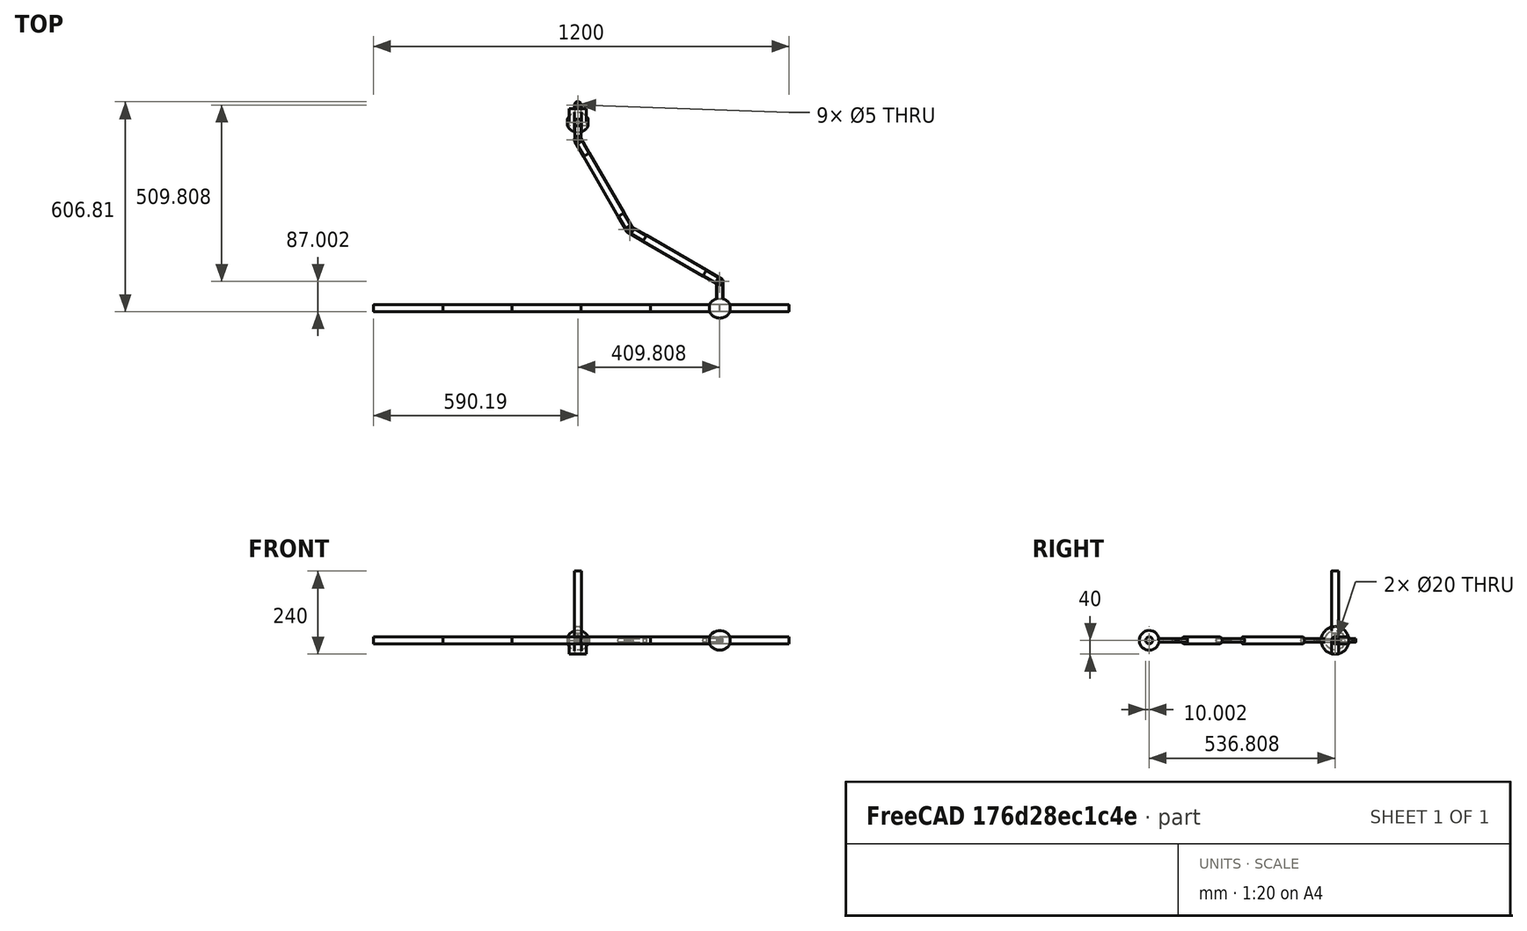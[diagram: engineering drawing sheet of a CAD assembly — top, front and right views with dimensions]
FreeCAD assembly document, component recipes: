
FREECAD ASSEMBLY — COMPONENT RECIPES ("Demo2Bodies")

This assembly document has 7 components, labeled P0..P6 below (a component is one placed body or linked part). 7 of them carry a construction recipe — the FreeCAD feature program that regenerates the part from scratch, quoted from this document or its linked companion documents; the rest are supplied as boundary geometry only. No exploded tour is included for this assembly.
COMPONENT P0 — recipe-attached ("Weight", modeled in this document).
Construction recipe (the document's own serialized feature program — sketch geometry with constraints, then the solid features built on it; lengths are millimeters unless a unit is written):

FEATURE [Sketcher::SketchObject] Sketch
  FullyConstrained = true
  MapMode = 5
  Support = -> [XY_Plane]
  sketch-geometry (2):
    g0: LineSegment StartX=-30 StartY=10 StartZ=0 EndX=30 EndY=10 EndZ=0
    g1: ArcOfCircle CenterX=0 CenterY=-5 CenterZ=0 NormalX=0 NormalY=0 NormalZ=1 AngleXU=0 Radius=33.541 StartAngle=0.463648 EndAngle=2.67795
  constraints (7):
    c: Horizontal(g0)
    c: DistanceY(g-1,g0) = 10
    c: DistanceX(g-1,g0) = 30
    c: PointOnObject(g1,g-2)
    c: DistanceY(g1,g-1) = 5
    c: Coincident(g1,g0)
    c: Coincident(g1,g0)
FEATURE [PartDesign::Revolution] Revolution
  Angle = 360
  Axis = (1,0,0)
  Base = (0,0,0)
  Profile = -> Sketch
  ReferenceAxis = -> Sketch [H_Axis]
FEATURE [PartDesign::CoordinateSystem] WeightTop
  AttacherType = Attacher::AttachEngine3D
  MapMode = 11
  Placement = pos=(30,-1.8e-15,0) rot=(0.707107,0,0.707107;3.14159rad)
  Support = -> [Revolution]
FEATURE [PartDesign::CoordinateSystem] WeightBot
  AttacherType = Attacher::AttachEngine3D
  MapMode = 11
  Placement = pos=(-30,0,0) rot=(0.707107,0,0.707107;3.14159rad)
  Support = -> [Revolution]
FEATURE [PartDesign::CoordinateSystem] WeightLCS
  AttacherType = Attacher::AttachEngine3D
  MapMode = 2
  Support = -> [Body003]
FEATURE [PartDesign::Body] Body  label="Weight"
  Group = -> [Sketch,Revolution,WeightLCS,WeightTop,WeightBot]
  Origin = -> Origin
  Tip = -> Revolution
COMPONENT P1 — recipe-attached ("Rod", modeled in this document).
Construction recipe (the document's own serialized feature program — sketch geometry with constraints, then the solid features built on it; lengths are millimeters unless a unit is written):

FEATURE [Sketcher::SketchObject] Sketch001
  FullyConstrained = true
  MapMode = 5
  Support = -> [XY_Plane001]
  sketch-geometry (1):
    g0: Circle CenterX=0 CenterY=0 CenterZ=0 NormalX=0 NormalY=0 NormalZ=1 AngleXU=0 Radius=10
  constraints (2):
    c: Coincident(g0,g-1)
    c: Diameter(g0) = 20
FEATURE [PartDesign::Pad] Pad
  Direction = (0,0,1)
  Length = 200
  Length2 = 10
  Profile = -> Sketch001
  ReferenceAxis = -> Sketch001 [N_Axis]
  Type = 0
FEATURE [PartDesign::CoordinateSystem] RodTop
  AttacherType = Attacher::AttachEngine3D
  MapMode = 11
  Placement = pos=(0,0,200) rot=(0,0,1;1.5708rad)
  Support = -> [Pad]
FEATURE [PartDesign::CoordinateSystem] RodBottom
  AttacherType = Attacher::AttachEngine3D
  MapMode = 11
  Placement = pos=(0,0,0) rot=(0,0,1;1.5708rad)
  Support = -> [Pad]
FEATURE [PartDesign::Body] Body001  label="Rod"
  Group = -> [Sketch001,Pad,RodTop,RodBottom]
  Origin = -> Origin001
  Tip = -> Pad
COMPONENT P2 — recipe-attached ("LugBody", modeled in this document).
Construction recipe (the document's own serialized feature program — sketch geometry with constraints, then the solid features built on it; lengths are millimeters unless a unit is written):

FEATURE [Sketcher::SketchObject] Sketch002
  FullyConstrained = true
  MapMode = 5
  Support = -> [XY_Plane002]
  sketch-geometry (5):
    g0: LineSegment StartX=-10 StartY=0 StartZ=0 EndX=-10 EndY=50 EndZ=0
    g1: ArcOfCircle CenterX=0 CenterY=50 CenterZ=0 NormalX=0 NormalY=0 NormalZ=1 AngleXU=0 Radius=10 StartAngle=1e-16 EndAngle=3.14159
    g2: LineSegment StartX=10 StartY=50 StartZ=0 EndX=10 EndY=0 EndZ=0
    g3: LineSegment StartX=10 StartY=0 StartZ=0 EndX=-10 EndY=0 EndZ=0
    g4: Circle CenterX=0 CenterY=50 CenterZ=0 NormalX=0 NormalY=0 NormalZ=1 AngleXU=0 Radius=2.5
  constraints (13):
    c: PointOnObject(g0,g-1)
    c: Vertical(g0)
    c: Tangent(g0,g1) = 1.5708
    c: Tangent(g1,g2) = 1.5708
    c: Coincident(g2,g3)
    c: Coincident(g3,g0)
    c: Horizontal(g3)
    c: PointOnObject(g1,g-2)
    c: Vertical(g2)
    c: Diameter(g1) = 20
    c: Distance(g2) = 50
    c: Coincident(g4,g1)
    c: Diameter(g4) = 5
FEATURE [PartDesign::Pad] Pad001
  Direction = (0,0,1)
  Length = 10
  Length2 = 10
  Midplane = true
  Profile = -> Sketch002
  ReferenceAxis = -> Sketch002 [N_Axis]
  Type = 0
FEATURE [PartDesign::Body] Body002  label="LugBody"
  Group = -> [Sketch002,Pad001]
  Origin = -> Origin002
  Tip = -> Pad001
COMPONENT P3 — recipe-attached ("LugCylinder", modeled in this document).
Construction recipe (the document's own serialized feature program — sketch geometry with constraints, then the solid features built on it; lengths are millimeters unless a unit is written):

FEATURE [Sketcher::SketchObject] Sketch003
  FullyConstrained = true
  MapMode = 5
  Placement = pos=(0,0,0) rot=(1,0,0;1.5708rad)
  Support = -> [XZ_Plane003]
  sketch-geometry (1):
    g0: Circle CenterX=0 CenterY=0 CenterZ=0 NormalX=0 NormalY=0 NormalZ=1 AngleXU=0 Radius=10
  constraints (2):
    c: Coincident(g0,g-1)
    c: Diameter(g0) = 20
FEATURE [PartDesign::Pad] Pad002
  Direction = (0,-1,-2e-16)
  Length = 60
  Length2 = 10
  Placement = pos=(0,0,0) rot=(1,0,0;1.5708rad)
  Profile = -> Sketch003
  ReferenceAxis = -> Sketch003 [N_Axis]
  Reversed = true
  Type = 0
FEATURE [PartDesign::Boolean] Boolean
  BaseFeature = -> Pad002
  Group = -> [Body002]
  Type = 2
FEATURE [PartDesign::CoordinateSystem] LugHole
  AttacherType = Attacher::AttachEngine3D
  MapMode = 11
  Placement = pos=(0,50,5) rot=(0,0,1;1.5708rad)
  Support = -> [Boolean]
FEATURE [PartDesign::CoordinateSystem] LugFace
  AttacherType = Attacher::AttachEngine3D
  MapMode = 5
  Placement = pos=(0,0,0) rot=(1,0,0;1.5708rad)
  Support = -> [Boolean]
FEATURE [PartDesign::CoordinateSystem] LugRot30
  AttacherType = Attacher::AttachEngine3D
  AttachmentOffset = pos=(0,0,0) rot=(0,0,1;0.523599rad)
  MapMode = 11
  Placement = pos=(0,50,5) rot=(0,0,1;2.0944rad)
  Support = -> [Boolean]
FEATURE [PartDesign::CoordinateSystem] LugRot60
  AttacherType = Attacher::AttachEngine3D
  AttachmentOffset = pos=(0,0,0) rot=(0,0,1;1.0472rad)
  MapMode = 11
  Placement = pos=(0,50,5) rot=(0,0,1;2.61799rad)
  Support = -> [Boolean]
FEATURE [PartDesign::Body] Body003  label="LugCylinder"
  Group = -> [Sketch003,Pad002,Boolean,LugHole,LugFace,LugRot30,LugRot60]
  Origin = -> Origin003
  Tip = -> Boolean
COMPONENT P4 — recipe-attached ("BobBody", modeled in this document).
Construction recipe (the document's own serialized feature program — sketch geometry with constraints, then the solid features built on it; lengths are millimeters unless a unit is written):

FEATURE [Sketcher::SketchObject] Sketch004
  FullyConstrained = true
  MapMode = 5
  Support = -> [XY_Plane004]
  sketch-geometry (4):
    g0: LineSegment StartX=-10 StartY=0 StartZ=0 EndX=-10 EndY=30 EndZ=0
    g1: ArcOfCircle CenterX=0 CenterY=30 CenterZ=0 NormalX=0 NormalY=0 NormalZ=1 AngleXU=0 Radius=10 StartAngle=2e-16 EndAngle=3.14159
    g2: LineSegment StartX=10 StartY=30 StartZ=0 EndX=10 EndY=0 EndZ=0
    g3: LineSegment StartX=10 StartY=0 StartZ=0 EndX=-10 EndY=0 EndZ=0
  constraints (11):
    c: PointOnObject(g0,g-1)
    c: Vertical(g0)
    c: Tangent(g0,g1) = 1.5708
    c: Tangent(g1,g2) = 1.5708
    c: Coincident(g2,g3)
    c: Coincident(g3,g0)
    c: Vertical(g2)
    c: PointOnObject(g1,g-2)
    c: Diameter(g1) = 20
    c: Distance(g0) = 30
    c: PointOnObject(g2,g-1)
FEATURE [PartDesign::Revolution] Revolution001
  Angle = 360
  Axis = (1,0,0)
  Base = (0,0,0)
  Profile = -> Sketch004
  ReferenceAxis = -> Sketch004 [H_Axis]
FEATURE [PartDesign::CoordinateSystem] BobBody  label="BobBody001"
  AttacherType = Attacher::AttachEngine3D
  MapMode = 11
  Placement = pos=(-10,0,0) rot=(0.707107,0,0.707107;3.14159rad)
  Support = -> [Revolution001]
FEATURE [PartDesign::Body] Body004  label="BobBody"
  Group = -> [Sketch004,Revolution001,BobBody]
  Origin = -> Origin004
  Tip = -> Revolution001
COMPONENT P5 — recipe-attached ("GroundBody", modeled in this document).
Construction recipe (the document's own serialized feature program — sketch geometry with constraints, then the solid features built on it; lengths are millimeters unless a unit is written):

FEATURE [Sketcher::SketchObject] Sketch005
  FullyConstrained = true
  MapMode = 5
  Support = -> [XY_Plane005]
  sketch-geometry (4):
    g0: LineSegment StartX=-25 StartY=10 StartZ=0 EndX=25 EndY=10 EndZ=0
    g1: LineSegment StartX=25 StartY=10 StartZ=0 EndX=25 EndY=-10 EndZ=0
    g2: LineSegment StartX=25 StartY=-10 StartZ=0 EndX=-25 EndY=-10 EndZ=0
    g3: LineSegment StartX=-25 StartY=-10 StartZ=0 EndX=-25 EndY=10 EndZ=0
  constraints (11):
    c: Coincident(g0,g1)
    c: Coincident(g1,g2)
    c: Coincident(g2,g3)
    c: Coincident(g3,g0)
    c: Horizontal(g0)
    c: Horizontal(g2)
    c: Vertical(g1)
    c: Vertical(g3)
    c: DistanceY(g2,g0) = 20
    c: DistanceX(g0,g0) = 50
    c: Symmetric(g0,g1,g-1)
FEATURE [PartDesign::Pad] Pad003
  Direction = (0,0,1)
  Length = 40
  Length2 = 10
  Profile = -> Sketch005
  ReferenceAxis = -> Sketch005 [N_Axis]
  Reversed = true
  Type = 0
FEATURE [PartDesign::CoordinateSystem] GroundLCS
  AttacherType = Attacher::AttachEngine3D
  MapMode = 5
  Placement = pos=(0,0,-40) rot=(1,0,0;3.14159rad)
  Support = -> [Pad003]
FEATURE [PartDesign::Body] Body005  label="GroundBody"
  Group = -> [Sketch005,Pad003,GroundLCS]
  Origin = -> Origin005
  Tip = -> Pad003
COMPONENT P6 — recipe-attached ("Spacer", modeled in this document).
Construction recipe (the document's own serialized feature program — sketch geometry with constraints, then the solid features built on it; lengths are millimeters unless a unit is written):

FEATURE [Sketcher::SketchObject] Sketch006
  FullyConstrained = true
  MapMode = 5
  Support = -> [XY_Plane007]
  sketch-geometry (2):
    g0: Circle CenterX=0 CenterY=0 CenterZ=0 NormalX=0 NormalY=0 NormalZ=1 AngleXU=0 Radius=10
    g1: Circle CenterX=0 CenterY=0 CenterZ=0 NormalX=0 NormalY=0 NormalZ=1 AngleXU=0 Radius=2.5
  constraints (4):
    c: Coincident(g0,g-1)
    c: Coincident(g1,g0)
    c: Diameter(g0) = 20
    c: Diameter(g1) = 5
FEATURE [PartDesign::Pad] Pad004
  Direction = (0,0,1)
  Length = 20
  Length2 = 10
  Profile = -> Sketch006
  ReferenceAxis = -> Sketch006 [N_Axis]
  Type = 0
FEATURE [PartDesign::CoordinateSystem] SpacerTop
  AttacherType = Attacher::AttachEngine3D
  MapMode = 11
  Placement = pos=(0,0,20) rot=(0,0,1;1.5708rad)
  Support = -> [Pad004]
FEATURE [PartDesign::Body] Body006  label="Spacer"
  Group = -> [Sketch006,Pad004,SpacerTop]
  Origin = -> Origin007
  Tip = -> Pad004
PROVENANCE & LICENSES
A FreeCAD (.FCStd) document from a public repository crawl; recipes are the document's own serialized feature recipes (and, for linked parts, companion documents' recipes).
License: gpl-3.0.
